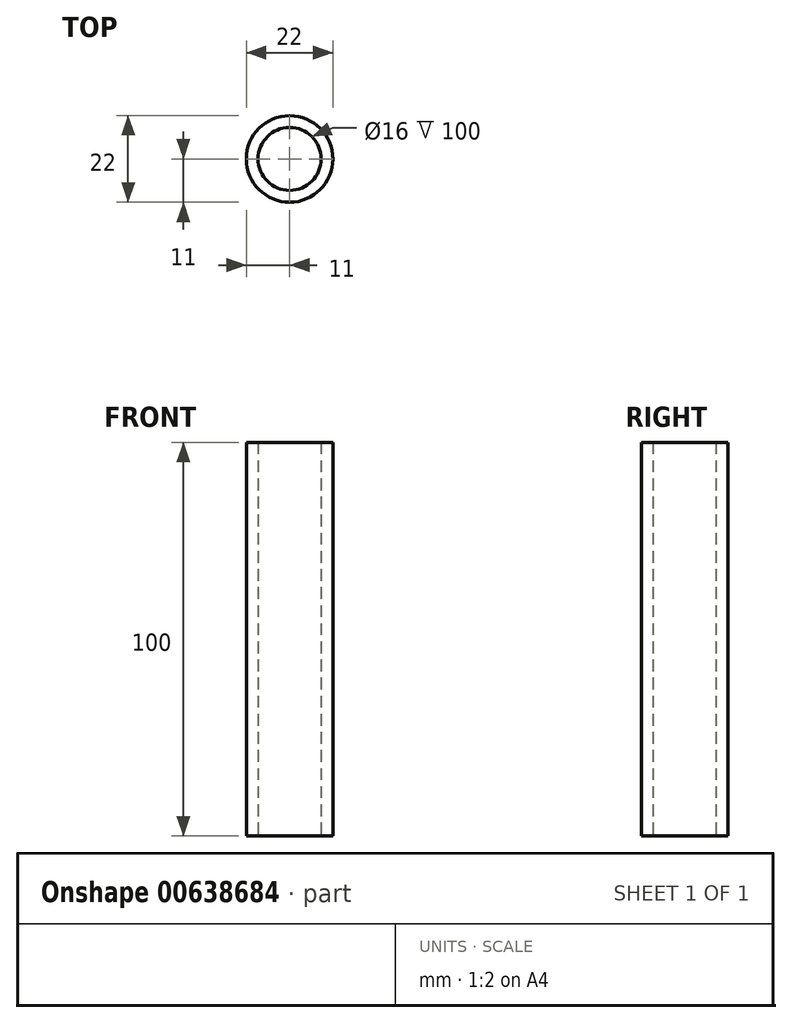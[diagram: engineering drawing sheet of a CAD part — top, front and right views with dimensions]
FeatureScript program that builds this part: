
annotation { "Feature Type Name" : "Feature", "Feature Type Description" : "" }
export const myFeature = defineFeature(function(context is Context, id is Id, definition is map)
    precondition{}
    {
        {
            var Q0;
            Q0=qCreatedBy(makeId("Top.planeOp"),FACE);
            var sketch = newSketch(context, id + "F0", { "sketchPlane" : qUnion([Q0])});
            skCircle(sketch, "E0", {"center": v(0, 0) * mm, "radius": 8 * mm});
            skCircle(sketch, "E1", {"center": v(0, 0) * mm, "radius": 11 * mm});
            skSolve(sketch);
        }
        {
            var Q0;
            Q0 = qSketchRegion(id + "F0", true);
            extrude(context, id + "F1", {"entities" : qUnion([Q0]), "depth" : 100 * mm, "offsetDistance" : 25 * mm});
        }
    });
